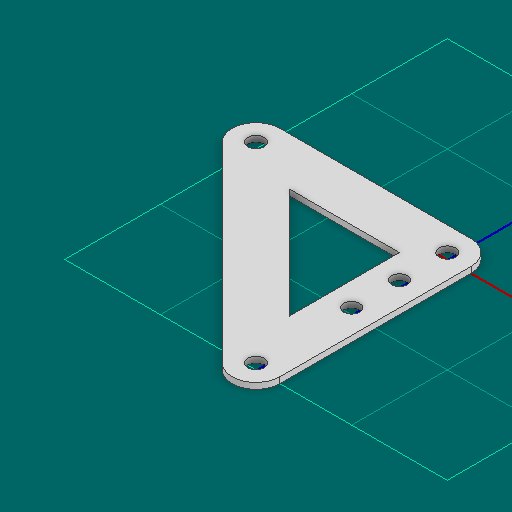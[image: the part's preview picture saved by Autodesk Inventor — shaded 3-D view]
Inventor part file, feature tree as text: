
AUTODESK INVENTOR PART (.ipt)
format: ipt  version: 2025 (Build 290162000, 162)  size: 118,272 bytes
history: native  units: in
note: dims shown in document units (in); Inventor stores cm internally (conversion verified against a paired STEP export)
features: other x3, extrude x1, sketch x1
ambient origin geometry x8: Origin, YZ Plane, XZ Plane, XY Plane, X Axis, Y Axis, Z Axis, Center Point
bodies: Solid1 (feature_tree)
feature tree (5):
  other  "Blocks"
  extrude  "Extrusion1"  Depth=0.0625in TaperAngle=0.0deg
  sketch  "Sketch1"  dims[d0=0.5in d1=0.5in d2=0.5in d3=0.0625in d4=0.0in d5=0.5in d6=0.165in d7=0.165in]
  other  "main"
  other  "main:1"
